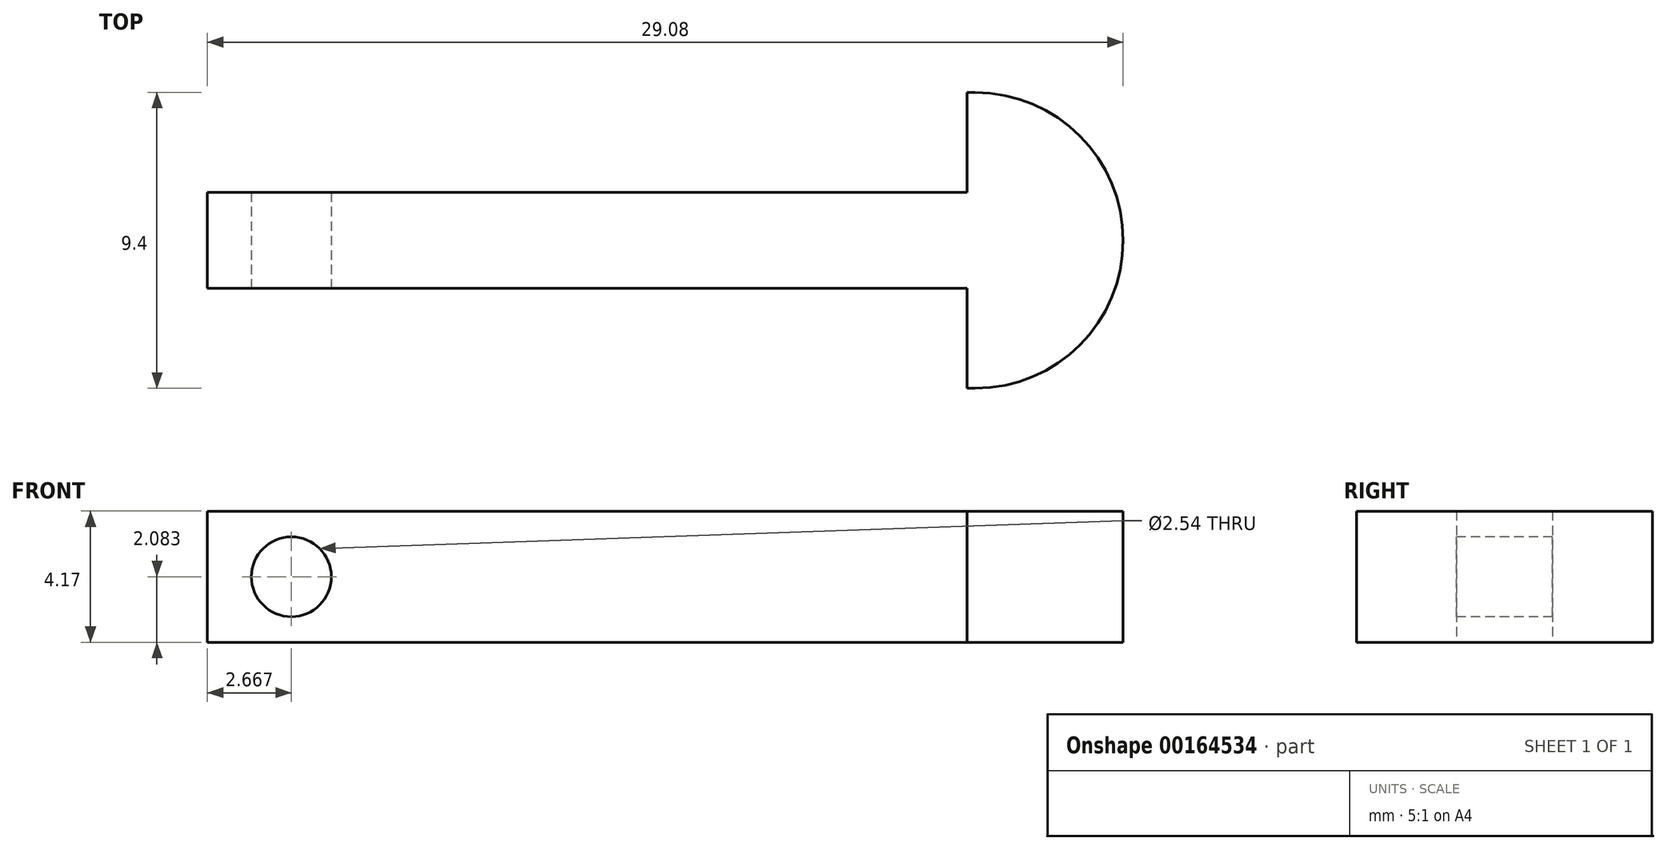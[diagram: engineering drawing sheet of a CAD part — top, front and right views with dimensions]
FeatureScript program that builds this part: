
annotation { "Feature Type Name" : "Feature", "Feature Type Description" : "" }
export const myFeature = defineFeature(function(context is Context, id is Id, definition is map)
    precondition{}
    {
        {
            var Q0;
            Q0=qCreatedBy(makeId("Top.planeOp"),FACE);
            var sketch = newSketch(context, id + "F0", { "sketchPlane" : qUnion([Q0])});
            skLineSegment(sketch, "E0", {"start": v(133.82, -1.52) * mm, "end": v(157.95, -1.52) * mm});
            skLineSegment(sketch, "E1", {"start": v(157.95, -1.52) * mm, "end": v(157.95, 0) * mm});
            skLineSegment(sketch, "E2", {"start": v(157.95, 0) * mm, "end": v(133.82, 0) * mm});
            skLineSegment(sketch, "E3", {"start": v(133.82, 0) * mm, "end": v(133.82, -1.52) * mm});
            skSolve(sketch);
        }
        {
            var Q0;
            Q0=qSketchRegion(id+"F0",true);
            extrude(context, id + "F1", {"entities" : qUnion([Q0]), "depth" : 4.17 * mm});
        }
        {
            var Q0;
            Q0=makeQuery(id+"F1.opExtrude","SWEPT_FACE",FACE,{"disambiguationData":[OSD([sQuery(id+"F0.wireOp",EDGE,"E1")])]});
            extrude(context, id + "F2", {"entities" : qUnion([Q0]), "depth" : 0.25 * mm});
        }
        {
            var Q0;
            Q0=makeQuery(id+"F2.opExtrude","SWEPT_FACE",FACE,{"disambiguationData":[OSD([sQuery(id+"F0.wireOp",EDGE,"E0"),sQuery(id+"F0.wireOp",EDGE,"E1")])]});
            extrude(context, id + "F3", {"entities" : qUnion([Q0]), "operationType" : NewBodyOperationType.ADD, "depth" : 3.17 * mm});
        }
        {
            var Q0;
            {var subQ0=sQuery(id+"F0.wireOp",EDGE,"E1");var subQ1=sQuery(id+"F0.wireOp",EDGE,"E0");Q0=makeQuery(id+"F3.boolean.opBoolean","MERGE",FACE,{"derivedFrom":[makeQuery(id+"F2.opExtrude","CAP_FACE",FACE,{"disambiguationData":[OSD([subQ0])],"isStart":false}),makeQuery(id+"F3.opExtrude","SWEPT_FACE",FACE,{"disambiguationData":[OSD([subQ1,subQ0]),TDD([makeQuery(id+"F2.opExtrude","CAP_EDGE",EDGE,{"disambiguationData":[OSD([subQ1,subQ0])],"isStart":false})])]})]});}
            var Q1;
            Q1=makeQuery(id+"F2.opExtrude","CAP_EDGE",EDGE,{"disambiguationData":[OSD([sQuery(id+"F0.wireOp",EDGE,"E1"),sQuery(id+"F0.wireOp",EDGE,"E2")])],"isStart":false});
            revolve(context, id + "F4", {"entities" : qUnion([Q0]), "axis" : qUnion([Q1]), "revolveType" : RevolveType.ONE_DIRECTION, "oppositeDirection" : true, "angle" : 90 * degree});
        }
        {
            var Q0;
            Q0=makeQuery(id+"F2.opExtrude","SWEPT_BODY",BODY,{"disambiguationData":[OSD([sQuery(id+"F0.wireOp",EDGE,"E1")])]});
            var Q1;
            Q1=makeQuery(id+"F1.opExtrude","SWEPT_BODY",BODY,{"disambiguationData":[OSD([sQuery(id+"F0.wireOp",EDGE,"E0"),sQuery(id+"F0.wireOp",EDGE,"E1"),sQuery(id+"F0.wireOp",EDGE,"E3"),sQuery(id+"F0.wireOp",EDGE,"E2")])]});
            var Q2;
            Q2=makeQuery(id+"F4.opRevolve","SWEPT_BODY",BODY,{"disambiguationData":[OSD([sQuery(id+"F0.wireOp",EDGE,"E0"),sQuery(id+"F0.wireOp",EDGE,"E1")])]});
            var Q3;
            Q3=qCreatedBy(makeId("Front.planeOp"),FACE);
            mirror(context, id + "F5", {"operationType" : NewBodyOperationType.ADD, "entities" : qUnion([Q0, Q1, Q2]), "mirrorPlane" : qUnion([Q3])});
        }
        {
            var Q0;
            Q0=makeQuery(id+"F1.opExtrude","SWEPT_FACE",FACE,{"disambiguationData":[OSD([sQuery(id+"F0.wireOp",EDGE,"E0")])]});
            var sketch = newSketch(context, id + "F6", { "sketchPlane" : qUnion([Q0])});
            skLineSegment(sketch, "E4", {"start": v(133.82, 2.08) * mm, "end": v(136.49, 2.08) * mm});
            skCircle(sketch, "E5", {"center": v(136.49, 2.08) * mm, "radius": 1.27 * mm});
            skSolve(sketch);
        }
        {
            var Q0;
            Q0 = qSketchRegion(id + "F6", true);
            extrude(context, id + "F7", {"entities" : qUnion([Q0]), "operationType" : NewBodyOperationType.REMOVE, "oppositeDirection" : true, "depth" : 25.4 * mm});
        }
    });
